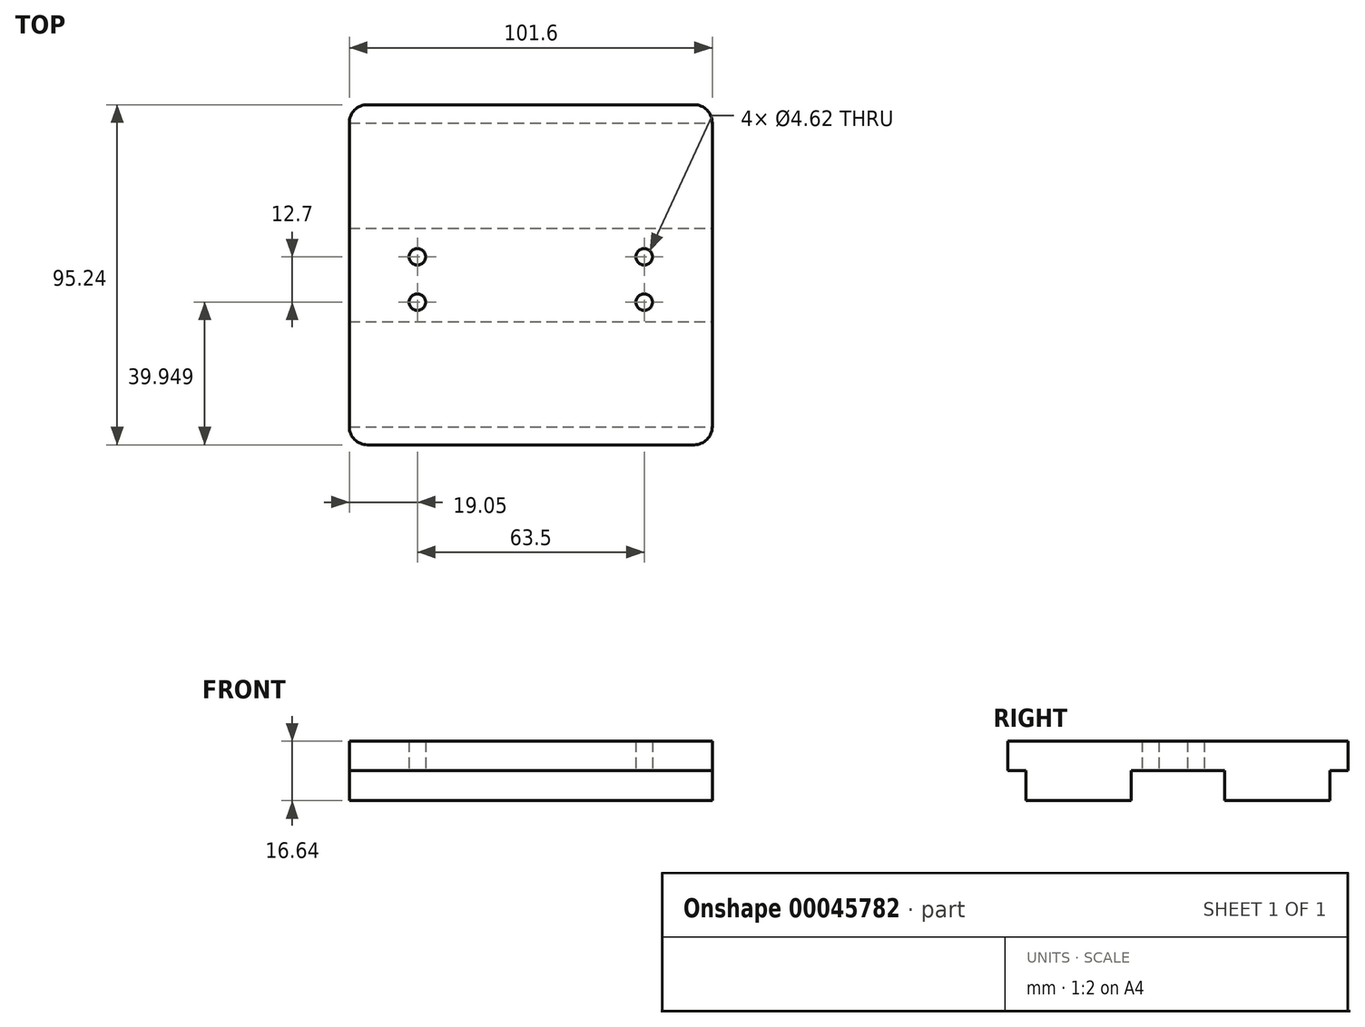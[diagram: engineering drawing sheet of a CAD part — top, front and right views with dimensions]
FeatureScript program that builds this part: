
annotation { "Feature Type Name" : "Feature", "Feature Type Description" : "" }
export const myFeature = defineFeature(function(context is Context, id is Id, definition is map)
    precondition{}
    {
        {
            var Q0;
            Q0=qCreatedBy(makeId("Top.planeOp"),FACE);
            var sketch = newSketch(context, id + "F0", { "sketchPlane" : qUnion([Q0])});
            skLineSegment(sketch, "E0.bottom", {"start": v(0, -15.24) * mm, "end": v(-38.1, -15.24) * mm});
            skLineSegment(sketch, "E0.top", {"start": v(0, 15.24) * mm, "end": v(-38.1, 15.24) * mm});
            skLineSegment(sketch, "E0.right", {"start": v(-38.1, -15.24) * mm, "end": v(-38.1, 15.24) * mm});
            skPoint(sketch, "E0.middle", {"position": v(0, 0) * mm});
            skLineSegment(sketch, "E1", {"start": v(-38.1, 15.24) * mm, "end": v(-25.4, 15.24) * mm});
            skCircle(sketch, "E2", {"center": v(-31.75, 5.03) * mm, "radius": 2.31 * mm});
            skCircle(sketch, "E3", {"center": v(-31.75, -7.67) * mm, "radius": 2.31 * mm});
            skLineSegment(sketch, "E4.MirrorCS", {"start": v(0, 15.24) * mm, "end": v(38.1, 15.24) * mm});
            skCircle(sketch, "E5.MirrorC", {"center": v(31.75, 5.03) * mm, "radius": 2.31 * mm});
            skLineSegment(sketch, "E6.MirrorCS", {"start": v(38.1, -15.24) * mm, "end": v(38.1, 15.24) * mm});
            skCircle(sketch, "E7.MirrorC", {"center": v(31.75, -7.67) * mm, "radius": 2.31 * mm});
            skLineSegment(sketch, "E8.MirrorCS", {"start": v(0, -15.24) * mm, "end": v(38.1, -15.24) * mm});
            skLineSegment(sketch, "E9.MirrorCS", {"start": v(38.1, 15.24) * mm, "end": v(25.4, 15.24) * mm});
            skLineSegment(sketch, "E10.bottom", {"start": v(50.8, -47.62) * mm, "end": v(-50.8, -47.63) * mm});
            skLineSegment(sketch, "E10.top", {"start": v(50.8, 47.63) * mm, "end": v(-50.8, 47.63) * mm});
            skLineSegment(sketch, "E10.left", {"start": v(50.8, -47.62) * mm, "end": v(50.8, 47.63) * mm});
            skLineSegment(sketch, "E10.right", {"start": v(-50.8, -47.63) * mm, "end": v(-50.8, 47.62) * mm});
            skSolve(sketch);
        }
        {
            var Q0;
            Q0=makeQuery(id+"F0.imprint","IMPRINT",FACE,{"disambiguationData":[TD([[makeQuery(id+"F0.imprint","IMPRINT",EDGE,{"derivedFrom":sQuery(id+"F0.wireOp",EDGE,"E0.bottom")}),-1.0]])]});
            var Q1;
            Q1=makeQuery(id+"F0.imprint","IMPRINT",FACE,{"disambiguationData":[TD([[makeQuery(id+"F0.imprint","IMPRINT",EDGE,{"derivedFrom":sQuery(id+"F0.wireOp",EDGE,"E0.bottom")}),1.0]])]});
            extrude(context, id + "F1", {"entities" : qUnion([Q0, Q1]), "depth" : 8.25 * mm});
        }
        {
            var Q0;
            Q0=makeQuery(id+"F1.opExtrude","SWEPT_EDGE",EDGE,{"disambiguationData":[OSD([sQuery(id+"F0.wireOp",EDGE,"E10.top"),sQuery(id+"F0.wireOp",EDGE,"E10.right")])]});
            var Q1;
            Q1=makeQuery(id+"F1.opExtrude","SWEPT_EDGE",EDGE,{"disambiguationData":[OSD([sQuery(id+"F0.wireOp",EDGE,"E10.top"),sQuery(id+"F0.wireOp",EDGE,"E10.left")])]});
            var Q2;
            Q2=makeQuery(id+"F1.opExtrude","SWEPT_EDGE",EDGE,{"disambiguationData":[OSD([sQuery(id+"F0.wireOp",EDGE,"E10.bottom"),sQuery(id+"F0.wireOp",EDGE,"E10.left")])]});
            var Q3;
            Q3=makeQuery(id+"F1.opExtrude","SWEPT_EDGE",EDGE,{"disambiguationData":[OSD([sQuery(id+"F0.wireOp",EDGE,"E10.bottom"),sQuery(id+"F0.wireOp",EDGE,"E10.right")])]});
            fillet(context, id + "F2", {"entities" : qUnion([Q0, Q1, Q2, Q3]), "radius" : 5.08 * mm, "tangentPropagation" : true, "allowEdgeOverflow" : false});
        }
        {
            var Q0;
            Q0=makeQuery(id+"F1.opExtrude","CAP_FACE",FACE,{"disambiguationData":[OSD([sQuery(id+"F0.wireOp",EDGE,"E2"),sQuery(id+"F0.wireOp",EDGE,"E3"),sQuery(id+"F0.wireOp",EDGE,"E5.MirrorC"),sQuery(id+"F0.wireOp",EDGE,"E7.MirrorC"),sQuery(id+"F0.wireOp",EDGE,"E10.bottom"),sQuery(id+"F0.wireOp",EDGE,"E10.top"),sQuery(id+"F0.wireOp",EDGE,"E10.left"),sQuery(id+"F0.wireOp",EDGE,"E10.right")])],"isStart":true});
            var sketch = newSketch(context, id + "F3", { "sketchPlane" : qUnion([Q0])});
            skLineSegment(sketch, "E11", {"start": v(-50.8, 42.55) * mm, "end": v(50.8, 42.54) * mm});
            skLineSegment(sketch, "E12", {"start": v(-50.8, -42.55) * mm, "end": v(50.8, -42.55) * mm});
            skLineSegment(sketch, "E13", {"start": v(-50.8, -13.08) * mm, "end": v(50.8, -13.08) * mm});
            skLineSegment(sketch, "E14", {"start": v(50.8, -13.08) * mm, "end": v(50.8, -42.55) * mm});
            skLineSegment(sketch, "E15", {"start": v(-50.8, 13.08) * mm, "end": v(50.8, 13.08) * mm});
            skLineSegment(sketch, "E16", {"start": v(50.8, 13.08) * mm, "end": v(50.8, 42.54) * mm});
            skSolve(sketch);
        }
        {
            var Q0;
            {var subQ1=sQuery(id+"F3.wireOp",EDGE,"ThryZmz4-NbBH-5noM-pw8m-Ug7i0lvmDzLx");Q0=makeQuery(id+"F3.imprint","IMPRINT",FACE,{"disambiguationData":[TD([[makeQuery(id+"F3.imprint","IMPRINT",EDGE,{"derivedFrom":subQ1}),-1.0]])]});}
            var Q1;
            {var subQ7=sQuery(id+"F3.wireOp",EDGE,"Zbw32KJ0-9u1Y-TgOT-PRb1-Vb3O8AMIQuOj");Q1=makeQuery(id+"F3.imprint","IMPRINT",FACE,{"disambiguationData":[TD([[makeQuery(id+"F3.imprint","IMPRINT",EDGE,{"derivedFrom":subQ7}),-1.0]])]});}
            var Q2;
            {var subQ0=sQuery(id+"F3.wireOp",EDGE,"E11");Q2=makeQuery(id+"F3.imprint","IMPRINT",FACE,{"disambiguationData":[TD([[makeQuery(id+"F3.imprint","IMPRINT",EDGE,{"derivedFrom":subQ0}),-1.0]])]});}
            var Q3;
            {var subQ0=sQuery(id+"F3.wireOp",EDGE,"E12");Q3=makeQuery(id+"F3.imprint","IMPRINT",FACE,{"disambiguationData":[TD([[makeQuery(id+"F3.imprint","IMPRINT",EDGE,{"derivedFrom":subQ0}),1.0]])]});}
            extrude(context, id + "F4", {"entities" : qUnion([Q0, Q1, Q2, Q3]), "operationType" : NewBodyOperationType.ADD, "depth" : 8.38 * mm});
        }
    });
